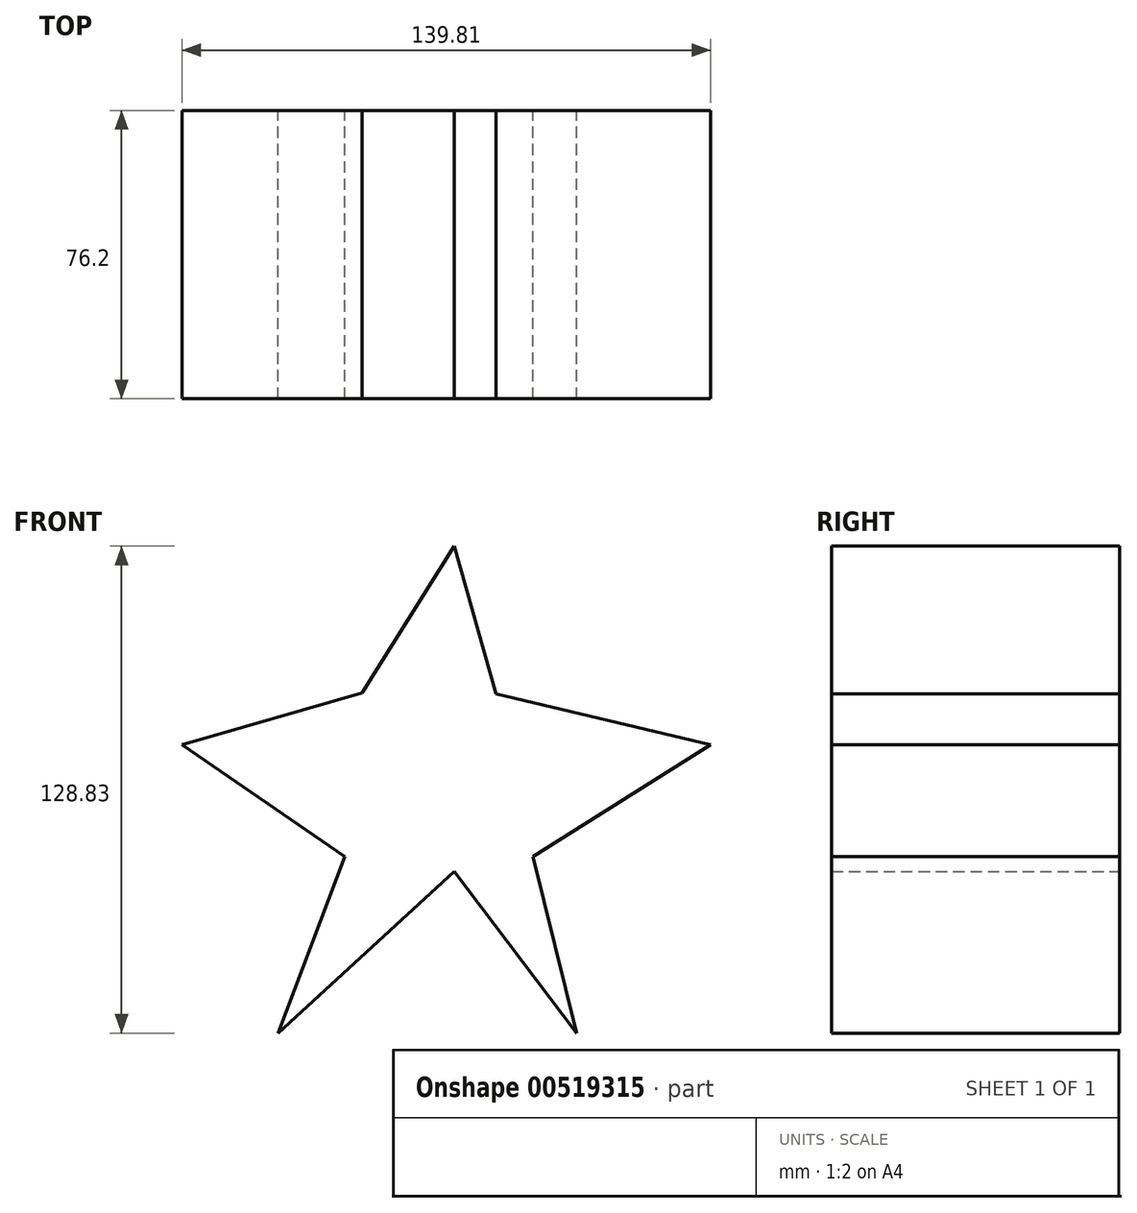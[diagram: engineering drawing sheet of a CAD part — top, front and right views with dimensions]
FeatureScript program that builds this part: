
annotation { "Feature Type Name" : "Feature", "Feature Type Description" : "" }
export const myFeature = defineFeature(function(context is Context, id is Id, definition is map)
    precondition{}
    {
        {
            var Q0;
            Q0=qCreatedBy(makeId("Front.planeOp"),FACE);
            var sketch = newSketch(context, id + "F0", { "sketchPlane" : qUnion([Q0])});
            skLineSegment(sketch, "E0", {"start": v(-76.01, 0) * mm, "end": v(-32.97, -29.61) * mm});
            skLineSegment(sketch, "E1", {"start": v(-32.97, -29.61) * mm, "end": v(-50.67, -76.32) * mm});
            skLineSegment(sketch, "E2", {"start": v(-50.67, -76.32) * mm, "end": v(-3.97, -33.58) * mm});
            skLineSegment(sketch, "E3", {"start": v(-3.97, -33.58) * mm, "end": v(28.39, -76.32) * mm});
            skLineSegment(sketch, "E4", {"start": v(28.39, -76.32) * mm, "end": v(16.79, -29.61) * mm});
            skLineSegment(sketch, "E5", {"start": v(16.79, -29.61) * mm, "end": v(63.8, 0) * mm});
            skLineSegment(sketch, "E6", {"start": v(63.8, 0) * mm, "end": v(7.02, 13.43) * mm});
            skLineSegment(sketch, "E7", {"start": v(-76.01, 0) * mm, "end": v(-28.39, 13.74) * mm});
            skLineSegment(sketch, "E8", {"start": v(-28.39, 13.74) * mm, "end": v(-3.97, 52.5) * mm});
            skLineSegment(sketch, "E9", {"start": v(-3.97, 52.5) * mm, "end": v(7.02, 13.43) * mm});
            skSolve(sketch);
        }
        {
            var Q0;
            Q0=makeQuery(id+"F0.imprint","IMPRINT",FACE,{"disambiguationData":[TD([[makeQuery(id+"F0.imprint","IMPRINT",EDGE,{"derivedFrom":sQuery(id+"F0.wireOp",EDGE,"E0")}),1.0]])]});
            extrude(context, id + "F1", {"entities" : qUnion([Q0]), "depth" : 76.2 * mm, "offsetDistance" : 25.4 * mm});
        }
    });
